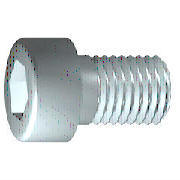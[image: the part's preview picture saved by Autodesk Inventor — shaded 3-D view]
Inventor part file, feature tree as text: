
AUTODESK INVENTOR PART (.ipt)
format: ipt  version: 2018 (Build 220112000, 112)  size: 185,856 bytes
history: native  units: mm (DEFAULTED — no unit token found)
features: sketch x2, extrude x1, plane x1, fillet x1
ambient origin geometry x7: Origin, YZ Plane, XY Plane, X Axis, Y Axis, Z Axis, Center Point
bodies: Solid1 (feature_tree), Body (feature_tree)
feature tree (5):
  extrude  "Slot"  Depth=4.0mm
  plane  "Work Plane1"
  fillet  "Fillet2"  Radius=4.0mm
  sketch  "Sketch1"  dims[d1=23.74117mm d2=0.429515mm d3=4.0mm]
  sketch  "Sketch2"  dims[d4=2.0mm d5=60.0deg d6=4.0mm d7=4.0mm d8=3.464102mm d9=7.0mm d10=90.0deg d11=10.0mm d12=0.0mm d13=23.74117mm d14=0.0mm d15=0.429415mm d16=0.429415mm d17=0.4mm d19=0.0mm d26=25.0mm d27=45.0deg d28=0.0mm d29=0.0mm d30=0.1mm]
